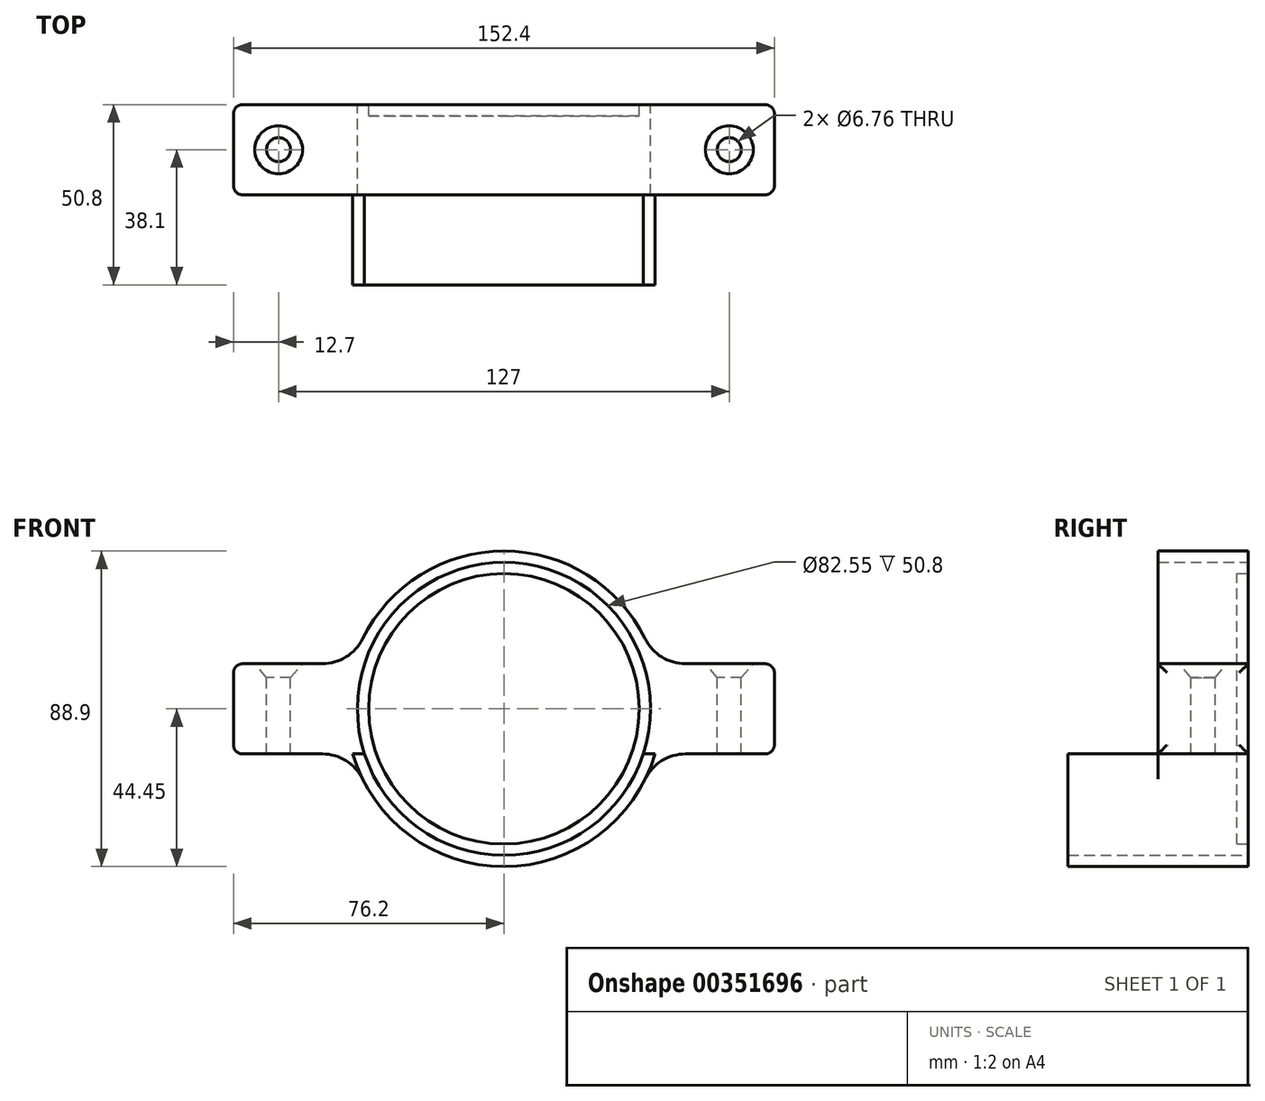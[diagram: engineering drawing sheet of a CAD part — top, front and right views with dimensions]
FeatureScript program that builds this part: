
annotation { "Feature Type Name" : "Feature", "Feature Type Description" : "" }
export const myFeature = defineFeature(function(context is Context, id is Id, definition is map)
    precondition{}
    {
        {
            var Q0;
            Q0=qCreatedBy(makeId("Front.planeOp"),FACE);
            var sketch = newSketch(context, id + "F0", { "sketchPlane" : qUnion([Q0])});
            skCircle(sketch, "E0", {"center": v(0, 0) * mm, "radius": 44.45 * mm});
            skLineSegment(sketch, "E1.bottom", {"start": v(-76.2, 12.7) * mm, "end": v(76.2, 12.7) * mm});
            skLineSegment(sketch, "E1.top", {"start": v(-76.2, -12.7) * mm, "end": v(76.2, -12.7) * mm});
            skLineSegment(sketch, "E1.left", {"start": v(-76.2, 12.7) * mm, "end": v(-76.2, -12.7) * mm});
            skLineSegment(sketch, "E1.right", {"start": v(76.2, 12.7) * mm, "end": v(76.2, -12.7) * mm});
            skSolve(sketch);
        }
        {
            var Q0;
            {var subQ0=sQuery(id+"F0.wireOp",EDGE,"E1.top");var subQ1=sQuery(id+"F0.wireOp",EDGE,"E0");var subQ2=makeQuery(id+"F0.imprint","INTERSECT",VERTEX,{"disambiguationData":[OD(0.0)],"derivedFrom":[subQ1,subQ0]});Q0=makeQuery(id+"F0.imprint","IMPRINT",FACE,{"disambiguationData":[TD([[makeQuery(id+"F0.imprint","IMPRINT",EDGE,{"disambiguationData":[TD([[subQ2,-1.0]])],"derivedFrom":subQ1}),1.0]])]});}
            extrude(context, id + "F1", {"entities" : qUnion([Q0]), "depth" : 50.8 * mm});
        }
        {
            var Q0;
            Q0 = qSketchRegion(id + "F0", true);
            extrude(context, id + "F2", {"entities" : qUnion([Q0]), "operationType" : NewBodyOperationType.ADD, "depth" : 25.4 * mm});
        }
        {
            var Q0;
            {var subQ0=sQuery(id+"F0.wireOp",EDGE,"E1.bottom");Q0=makeQuery(id+"F2.opExtrude","SWEPT_FACE",FACE,{"disambiguationData":[OSD([subQ0]),TDD([makeQuery(id+"F0.imprint","IMPRINT",EDGE,{"disambiguationData":[TD([[makeQuery(id+"F0.imprint","INTERSECT",VERTEX,{"derivedFrom":[subQ0,sQuery(id+"F0.wireOp",EDGE,"E1.left")]}),-1.0]])],"derivedFrom":subQ0})])]});}
            var sketch = newSketch(context, id + "F3", { "sketchPlane" : qUnion([Q0])});
            skCircle(sketch, "E2", {"center": v(-63.5, -12.7) * mm, "radius": 6.35 * mm});
            skCircle(sketch, "E3.MirrorC", {"center": v(63.5, -12.7) * mm, "radius": 6.35 * mm});
            skSolve(sketch);
        }
        {
            var Q0;
            Q0=sQuery(id+"F3.wireOp",VERTEX,"E2.center");
            var Q1;
            Q1=sQuery(id+"F3.wireOp",VERTEX,"E3.MirrorC.center");
            var Q2;
            Q2=makeQuery(id+"F1.opExtrude","SWEPT_BODY",BODY,{"disambiguationData":[OSD([sQuery(id+"F0.wireOp",EDGE,"E0"),sQuery(id+"F0.wireOp",EDGE,"E1.top")])]});
            hole(context, id + "F4", {"style" : HoleStyle.C_SINK, "endStyle" : HoleEndStyle.THROUGH, "standardTappedOrClearance" : lookupTablePath({ "standard" : "ANSI", "fit" : "Normal (ASME)", "size" : "1/4", "type" : "Clearance" }), "standardBlindInLast" : lookupTablePath({ "fit" : "Free", "standard" : "ANSI", "size" : "1/4", "type" : "Clearance" }), "holeDiameter" : 6.76 * mm, "cSinkDiameter" : 13.5 * mm, "cSinkAngle" : 82 * degree, "isTappedThrough" : true, "tappedDepth" : 12.7 * mm, "tapClearance" : 3, "startFromSketch" : true, "locations" : qUnion([Q0, Q1]), "scope" : qUnion([Q2])});
        }
        {
            var Q0;
            {var subQ0=sQuery(id+"F0.wireOp",EDGE,"E1.top");var subQ1=sQuery(id+"F0.wireOp",EDGE,"E0");var subQ2=makeQuery(id+"F0.imprint","INTERSECT",VERTEX,{"disambiguationData":[OD(0.0)],"derivedFrom":[subQ1,subQ0]});Q0=makeQuery(id+"F2.boolean.opBoolean","MERGE",EDGE,{"derivedFrom":[makeQuery(id+"F1.opExtrude","SWEPT_EDGE",EDGE,{"disambiguationData":[OSD([subQ1,subQ0]),TDD([subQ2])]}),makeQuery(id+"F2.opExtrude","SWEPT_EDGE",EDGE,{"disambiguationData":[OSD([subQ1,subQ0]),TDD([subQ2])]})]});}
            var Q1;
            {var subQ0=sQuery(id+"F0.wireOp",EDGE,"E1.top");var subQ1=sQuery(id+"F0.wireOp",EDGE,"E0");var subQ2=makeQuery(id+"F0.imprint","INTERSECT",VERTEX,{"disambiguationData":[OD(1.0)],"derivedFrom":[subQ1,subQ0]});Q1=makeQuery(id+"F2.boolean.opBoolean","MERGE",EDGE,{"derivedFrom":[makeQuery(id+"F1.opExtrude","SWEPT_EDGE",EDGE,{"disambiguationData":[OSD([subQ1,subQ0]),TDD([subQ2])]}),makeQuery(id+"F2.opExtrude","SWEPT_EDGE",EDGE,{"disambiguationData":[OSD([subQ1,subQ0]),TDD([subQ2])]})]});}
            var Q2;
            {var subQ0=sQuery(id+"F0.wireOp",EDGE,"E1.bottom");var subQ1=sQuery(id+"F0.wireOp",EDGE,"E0");Q2=makeQuery(id+"F2.opExtrude","SWEPT_EDGE",EDGE,{"disambiguationData":[OSD([subQ1,subQ0]),TDD([makeQuery(id+"F0.imprint","INTERSECT",VERTEX,{"disambiguationData":[OD(1.0)],"derivedFrom":[subQ1,subQ0]})])]});}
            var Q3;
            {var subQ0=sQuery(id+"F0.wireOp",EDGE,"E1.bottom");var subQ1=sQuery(id+"F0.wireOp",EDGE,"E0");Q3=makeQuery(id+"F2.opExtrude","SWEPT_EDGE",EDGE,{"disambiguationData":[OSD([subQ1,subQ0]),TDD([makeQuery(id+"F0.imprint","INTERSECT",VERTEX,{"disambiguationData":[OD(0.0)],"derivedFrom":[subQ1,subQ0]})])]});}
            fillet(context, id + "F5", {"entities" : qUnion([Q0, Q1, Q2, Q3]), "radius" : 12.7 * mm, "tangentPropagation" : true, "allowEdgeOverflow" : false});
        }
        {
            var Q0;
            Q0=makeQuery(id+"F2.opExtrude","CAP_EDGE",EDGE,{"disambiguationData":[OSD([sQuery(id+"F0.wireOp",EDGE,"E1.left")])],"isStart":false});
            var Q1;
            Q1=makeQuery(id+"F2.opExtrude","SWEPT_FACE",FACE,{"disambiguationData":[OSD([sQuery(id+"F0.wireOp",EDGE,"E1.left")])]});
            var Q2;
            Q2=makeQuery(id+"F2.opExtrude","SWEPT_EDGE",EDGE,{"disambiguationData":[OSD([sQuery(id+"F0.wireOp",EDGE,"E1.bottom"),sQuery(id+"F0.wireOp",EDGE,"E1.right")])]});
            var Q3;
            Q3=makeQuery(id+"F2.opExtrude","SWEPT_FACE",FACE,{"disambiguationData":[OSD([sQuery(id+"F0.wireOp",EDGE,"E1.right")])]});
            fillet(context, id + "F6", {"entities" : qUnion([Q0, Q1, Q2, Q3]), "radius" : 2.54 * mm, "tangentPropagation" : true, "allowEdgeOverflow" : false});
        }
        {
            var Q0;
            {var subQ0=sQuery(id+"F0.wireOp",EDGE,"E1.top");var subQ1=sQuery(id+"F0.wireOp",EDGE,"E0");Q0=makeQuery(id+"F2.boolean.opBoolean","MERGE",FACE,{"derivedFrom":[makeQuery(id+"F1.opExtrude","CAP_FACE",FACE,{"disambiguationData":[OSD([subQ1,subQ0])],"isStart":true}),makeQuery(id+"F2.opExtrude","CAP_FACE",FACE,{"disambiguationData":[OSD([subQ1,sQuery(id+"F0.wireOp",EDGE,"E1.bottom"),subQ0,sQuery(id+"F0.wireOp",EDGE,"E1.left"),sQuery(id+"F0.wireOp",EDGE,"E1.right")])],"isStart":true})]});}
            var sketch = newSketch(context, id + "F7", { "sketchPlane" : qUnion([Q0])});
            skCircle(sketch, "E4", {"center": v(0, 0) * mm, "radius": 41.28 * mm});
            skSolve(sketch);
        }
        {
            var Q0;
            Q0 = qSketchRegion(id + "F7", true);
            extrude(context, id + "F8", {"entities" : qUnion([Q0]), "operationType" : NewBodyOperationType.REMOVE, "endBound" : BoundingType.SYMMETRIC, "oppositeDirection" : true, "depth" : 144.78 * mm});
        }
        {
            var Q0;
            Q0=qCreatedBy(makeId("Front.planeOp"),FACE);
            var sketch = newSketch(context, id + "F9", { "sketchPlane" : qUnion([Q0])});
            skCircle(sketch, "E5", {"center": v(0, 0) * mm, "radius": 38.1 * mm});
            skSolve(sketch);
        }
        {
            var Q0;
            Q0=makeQuery(id+"F9.imprint","IMPRINT",FACE,{"disambiguationData":[TD([[makeQuery(id+"F9.imprint","IMPRINT",EDGE,{"derivedFrom":sQuery(id+"F9.wireOp",EDGE,"E5")}),1.0]])]});
            extrude(context, id + "F10", {"entities" : qUnion([Q0]), "depth" : 3.17 * mm});
        }
    });
